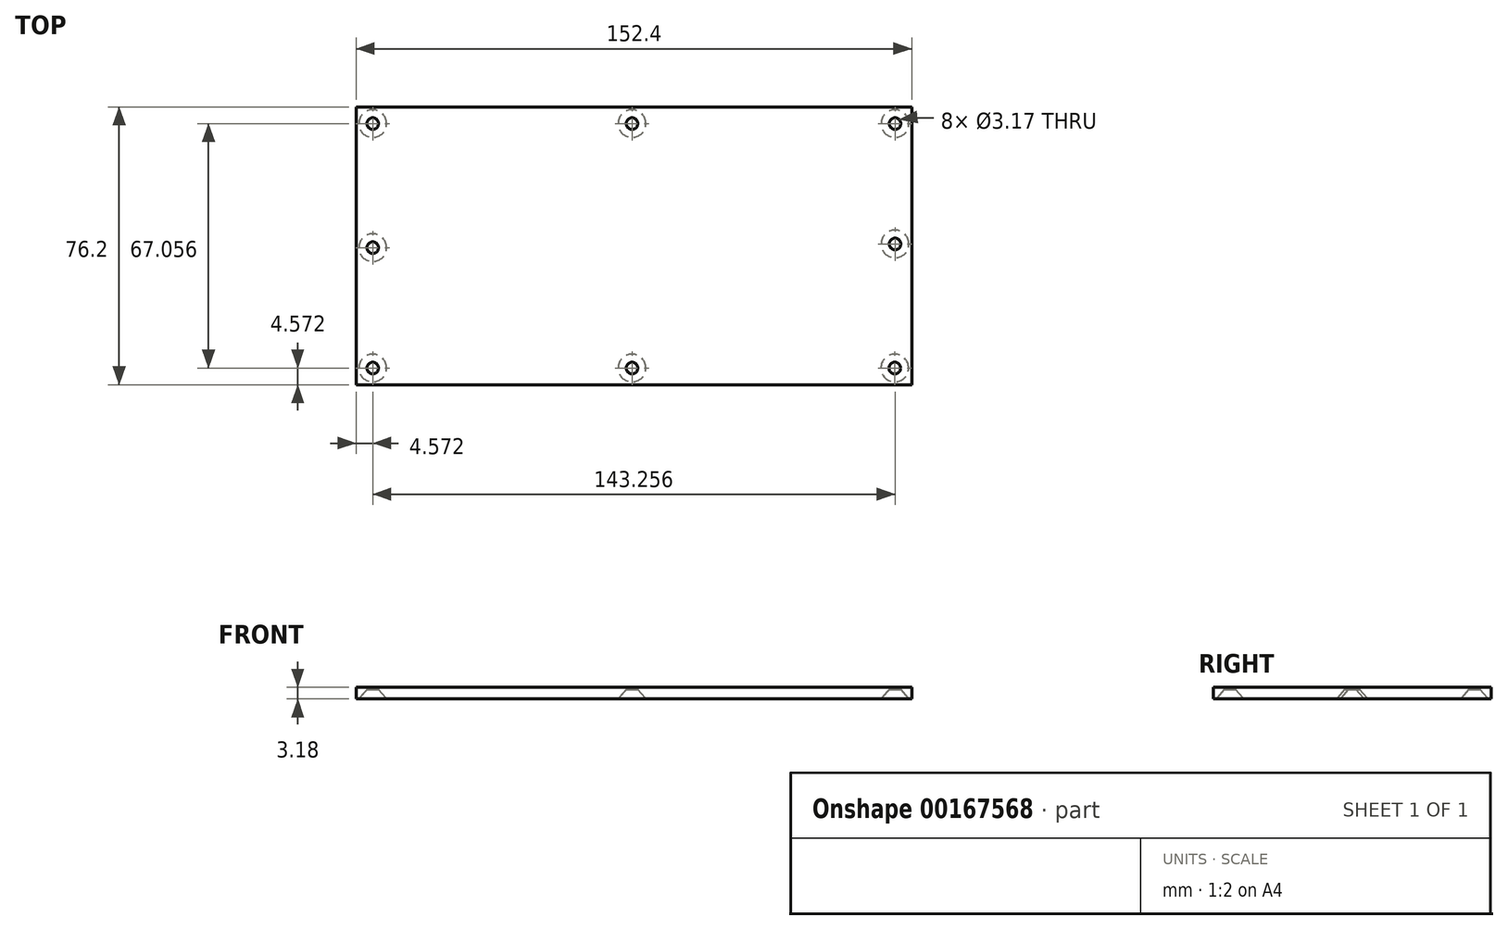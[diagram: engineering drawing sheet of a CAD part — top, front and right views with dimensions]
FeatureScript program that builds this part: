
annotation { "Feature Type Name" : "Feature", "Feature Type Description" : "" }
export const myFeature = defineFeature(function(context is Context, id is Id, definition is map)
    precondition{}
    {
        {
            var Q0;
            Q0=qCreatedBy(makeId("Top.planeOp"),FACE);
            var sketch = newSketch(context, id + "F0", { "sketchPlane" : qUnion([Q0])});
            skLineSegment(sketch, "E0.bottom", {"start": v(0, 0) * mm, "end": v(152.4, 0) * mm});
            skLineSegment(sketch, "E0.top", {"start": v(0, 76.2) * mm, "end": v(152.4, 76.2) * mm});
            skLineSegment(sketch, "E0.left", {"start": v(0, 0) * mm, "end": v(0, 76.2) * mm});
            skLineSegment(sketch, "E0.right", {"start": v(152.4, 0) * mm, "end": v(152.4, 76.2) * mm});
            skSolve(sketch);
        }
        {
            var Q0;
            Q0=qSketchRegion(id+"F0",true);
            extrude(context, id + "F1", {"entities" : qUnion([Q0]), "depth" : 3.17 * mm});
        }
        {
            var Q0;
            Q0=makeQuery(id+"F1.opExtrude","CAP_FACE",FACE,{"disambiguationData":[OSD([sQuery(id+"F0.wireOp",EDGE,"E0.bottom"),sQuery(id+"F0.wireOp",EDGE,"E0.top"),sQuery(id+"F0.wireOp",EDGE,"E0.left"),sQuery(id+"F0.wireOp",EDGE,"E0.right")])],"isStart":true});
            var sketch = newSketch(context, id + "F2", { "sketchPlane" : qUnion([Q0])});
            skPoint(sketch, "E1", {"position": v(4.57, -4.57) * mm});
            skPoint(sketch, "E2", {"position": v(4.57, -71.63) * mm});
            skPoint(sketch, "E3", {"position": v(147.83, -71.63) * mm});
            skPoint(sketch, "E4", {"position": v(147.83, -457.2) * mm});
            skPoint(sketch, "E5", {"position": v(75.7, -71.63) * mm});
            skPoint(sketch, "E6", {"position": v(75.7, -4.57) * mm});
            skPoint(sketch, "E7", {"position": v(4.57, -37.6) * mm});
            skPoint(sketch, "E8", {"position": v(147.83, -38.6) * mm});
            skPoint(sketch, "E9", {"position": v(147.76, -4.57) * mm});
            skSolve(sketch);
        }
        {
            var Q0;
            Q0=sQuery(id+"F2.wireOp",VERTEX,"E1");
            var Q1;
            Q1=sQuery(id+"F2.wireOp",VERTEX,"E7");
            var Q2;
            Q2=sQuery(id+"F2.wireOp",VERTEX,"E2");
            var Q3;
            Q3=sQuery(id+"F2.wireOp",VERTEX,"E5");
            var Q4;
            Q4=sQuery(id+"F2.wireOp",VERTEX,"E3");
            var Q5;
            Q5=sQuery(id+"F2.wireOp",VERTEX,"E8");
            var Q6;
            Q6=sQuery(id+"F2.wireOp",VERTEX,"E4");
            var Q7;
            Q7=sQuery(id+"F2.wireOp",VERTEX,"E6");
            var Q8;
            Q8=sQuery(id+"F2.wireOp",VERTEX,"E9");
            var Q9;
            Q9=makeQuery(id+"F1.opExtrude","SWEPT_BODY",BODY,{"disambiguationData":[OSD([sQuery(id+"F0.wireOp",EDGE,"E0.bottom"),sQuery(id+"F0.wireOp",EDGE,"E0.top"),sQuery(id+"F0.wireOp",EDGE,"E0.left"),sQuery(id+"F0.wireOp",EDGE,"E0.right")])]});
            hole(context, id + "F3", {"style" : HoleStyle.C_SINK, "endStyle" : HoleEndStyle.THROUGH, "holeDiameter" : 3.17 * mm, "cSinkDiameter" : 7.62 * mm, "cSinkAngle" : 82 * degree, "locations" : qUnion([Q0, Q1, Q2, Q3, Q4, Q5, Q6, Q7, Q8]), "scope" : qUnion([Q9]), "isTappedThrough" : true});
        }
    });
